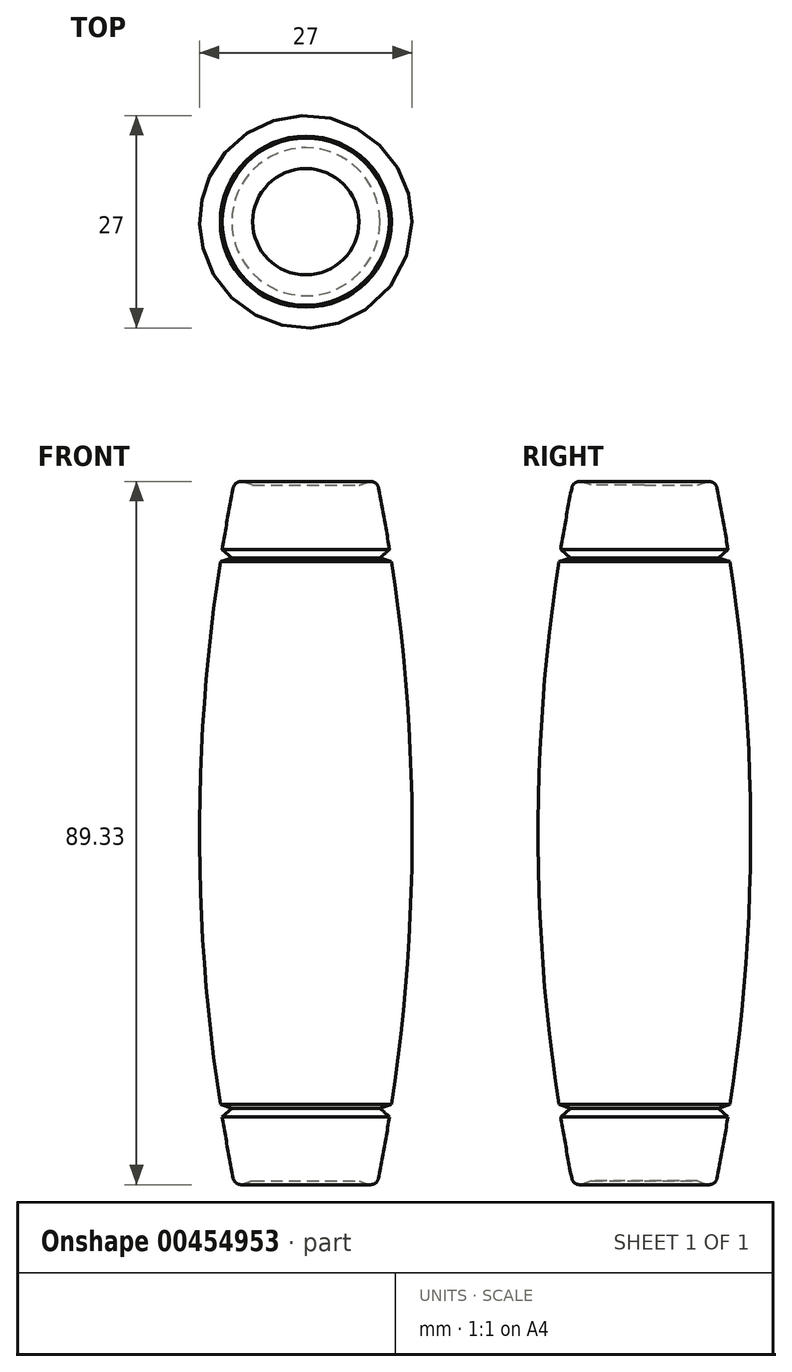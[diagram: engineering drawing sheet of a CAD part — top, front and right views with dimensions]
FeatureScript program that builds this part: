
annotation { "Feature Type Name" : "Feature", "Feature Type Description" : "" }
export const myFeature = defineFeature(function(context is Context, id is Id, definition is map)
    precondition{}
    {
        {
            var Q0;
            Q0=qCreatedBy(makeId("Front.planeOp"),FACE);
            var sketch = newSketch(context, id + "F0", { "sketchPlane" : qUnion([Q0])});
            skLineSegment(sketch, "E0", {"start": v(0, 0) * mm, "end": v(0, 88.37) * mm, "construction": true});
            skArc(sketch, "E1", {"start": v(9, -0.82) * mm, "mid": v(13.5, 44.18) * mm, "end": v(9, 89.18) * mm});
            skLineSegment(sketch, "E2", {"start": v(-213.5, 44.18) * mm, "end": v(0, 44.18) * mm, "construction": true});
            skLineSegment(sketch, "E3", {"start": v(13.5, 44.18) * mm, "end": v(13.5, 17.37) * mm, "construction": true});
            skLineSegment(sketch, "E4", {"start": v(0, 0) * mm, "end": v(0, 88.37) * mm});
            skLineSegment(sketch, "E5", {"start": v(9, 89.18) * mm, "end": v(-10.02, 89.18) * mm, "construction": true});
            skLineSegment(sketch, "E6", {"start": v(9, -0.82) * mm, "end": v(-18, -0.82) * mm, "construction": true});
            skLineSegment(sketch, "E7", {"start": v(0, 88.37) * mm, "end": v(33.92, 88.37) * mm, "construction": true});
            skLineSegment(sketch, "E8", {"start": v(0, 0) * mm, "end": v(42, 0) * mm, "construction": true});
            skLineSegment(sketch, "E9", {"start": v(0, 88.37) * mm, "end": v(6.75, 88.37) * mm});
            skLineSegment(sketch, "E10", {"start": v(6.75, 88.37) * mm, "end": v(9, 89.18) * mm});
            skLineSegment(sketch, "E11", {"start": v(0, 0) * mm, "end": v(6.75, 0) * mm});
            skLineSegment(sketch, "E12", {"start": v(6.75, 0) * mm, "end": v(9, -0.82) * mm});
            skSolve(sketch);
        }
        {
            var Q0;
            Q0=makeQuery(id+"F0.imprint","IMPRINT",FACE,{"disambiguationData":[TD([[makeQuery(id+"F0.imprint","IMPRINT",EDGE,{"derivedFrom":sQuery(id+"F0.wireOp",EDGE,"E1")}),1.0]])]});
            var Q1;
            Q1=sQuery(id+"F0.wireOp",EDGE,"E4");
            revolve(context, id + "F1", {"entities" : qUnion([Q0]), "axis" : qUnion([Q1]), "revolveType" : RevolveType.FULL});
        }
        {
            var Q0;
            Q0=makeQuery(id+"F1.opRevolve","SWEPT_EDGE",EDGE,{"disambiguationData":[OSD([sQuery(id+"F0.wireOp",EDGE,"E1"),sQuery(id+"F0.wireOp",EDGE,"oIb8xYxR-XwdV-IQJ0-qUSZ-DkgYWBHBJ82f")])]});
            var Q1;
            Q1=makeQuery(id+"F1.opRevolve","SWEPT_EDGE",EDGE,{"disambiguationData":[OSD([sQuery(id+"F0.wireOp",EDGE,"E1"),sQuery(id+"F0.wireOp",EDGE,"766e9889-5059-467a-8efe-476706b1f5470.MirrorCS")])]});
            fillet(context, id + "F2", {"entities" : qUnion([Q0, Q1]), "radius" : 1 * mm, "tangentPropagation" : true, "allowEdgeOverflow" : false});
        }
        {
            var Q0;
            Q0=qCreatedBy(makeId("Front.planeOp"),FACE);
            var sketch = newSketch(context, id + "F3", { "sketchPlane" : qUnion([Q0])});
            skArc(sketch, "E13", {"start": v(-8.04, 89.02) * mm, "mid": v(0, 88.37) * mm, "end": v(8.04, 89.02) * mm, "construction": true});
            skArc(sketch, "E14", {"start": v(8.04, -0.65) * mm, "mid": v(0, 0) * mm, "end": v(-8.04, -0.65) * mm, "construction": true});
            skLineSegment(sketch, "E15", {"start": v(8.04, 89.02) * mm, "end": v(8.04, -0.65) * mm, "construction": true});
            skLineSegment(sketch, "E16", {"start": v(8.04, 44.18) * mm, "end": v(-31.5, 44.18) * mm, "construction": true});
            skLineSegment(sketch, "E17", {"start": v(14.73, 83.85) * mm, "end": v(9.4, 79.14) * mm});
            skLineSegment(sketch, "E18", {"start": v(9.4, 79.14) * mm, "end": v(17.61, 76.39) * mm});
            skLineSegment(sketch, "E19", {"start": v(14.73, 83.85) * mm, "end": v(17.61, 76.39) * mm});
            skLineSegment(sketch, "E20.MirrorCS", {"start": v(14.73, 4.52) * mm, "end": v(9.4, 9.23) * mm});
            skLineSegment(sketch, "E21.MirrorCS", {"start": v(9.4, 9.23) * mm, "end": v(17.61, 11.98) * mm});
            skLineSegment(sketch, "E22.MirrorCS", {"start": v(14.73, 4.52) * mm, "end": v(17.61, 11.98) * mm});
            skLineSegment(sketch, "E23", {"start": v(0, 0) * mm, "end": v(0, 55.62) * mm, "construction": true});
            skSolve(sketch);
        }
        {
            var Q0;
            Q0=qSketchRegion(id+"F3",true);
            var Q1;
            Q1=sQuery(id+"F3.wireOp",EDGE,"E23");
            revolve(context, id + "F4", {"operationType" : NewBodyOperationType.REMOVE, "entities" : qUnion([Q0]), "axis" : qUnion([Q1]), "revolveType" : RevolveType.FULL, "oppositeDirection" : true});
        }
    });
